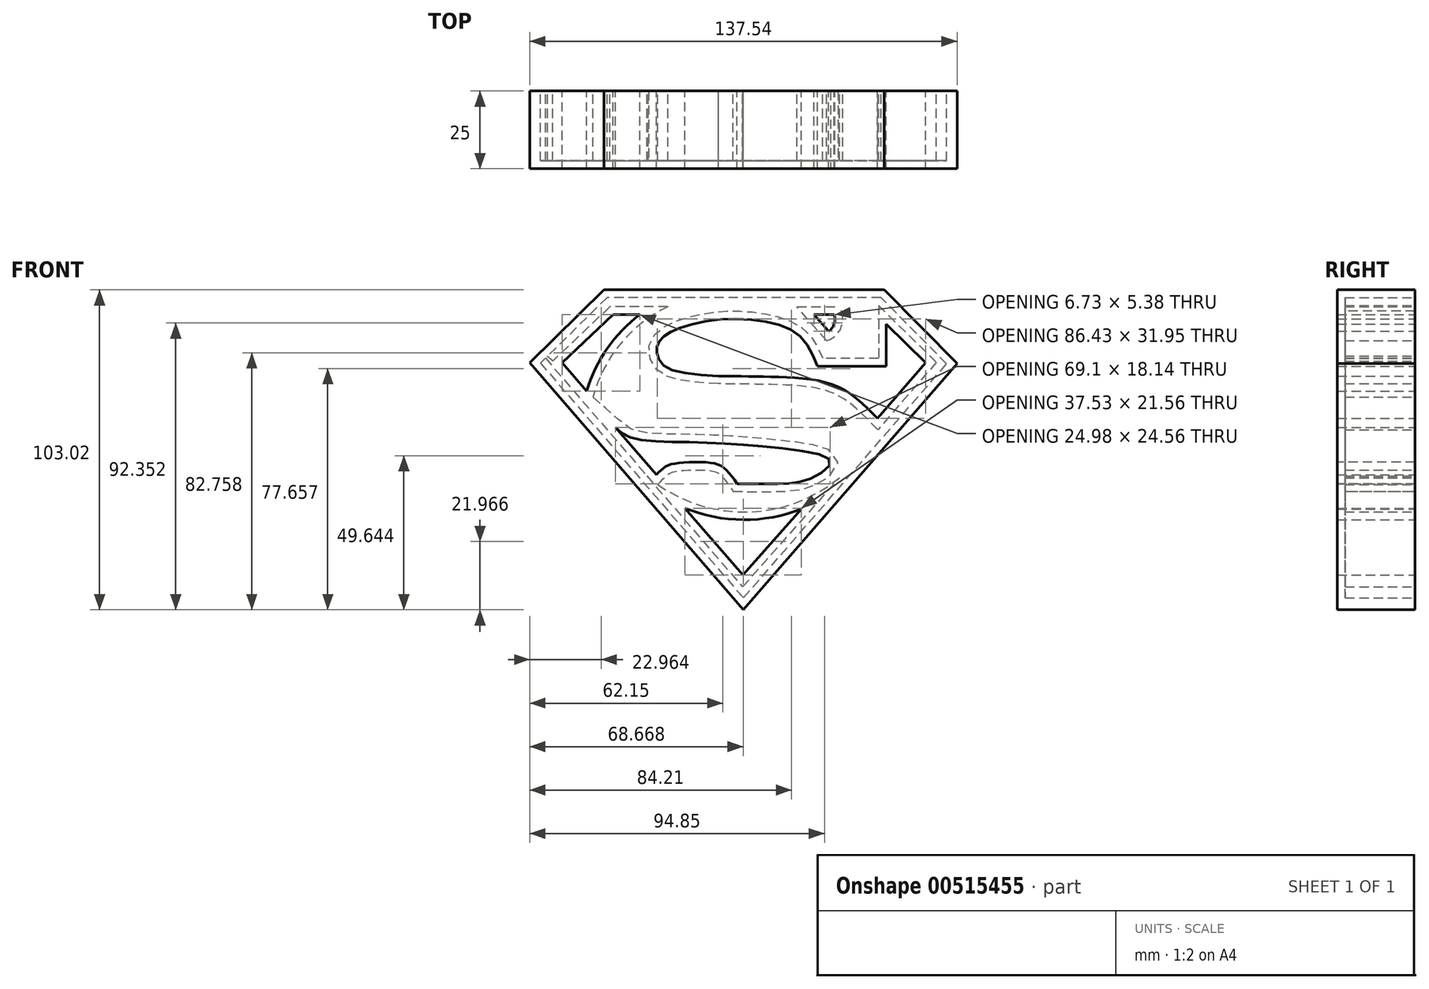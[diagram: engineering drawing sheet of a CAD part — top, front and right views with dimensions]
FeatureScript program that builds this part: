
annotation { "Feature Type Name" : "Feature", "Feature Type Description" : "" }
export const myFeature = defineFeature(function(context is Context, id is Id, definition is map)
    precondition{}
    {
        {
            var Q0;
            Q0=qCreatedBy(makeId("Front.planeOp"),FACE);
            var sketch = newSketch(context, id + "F0", { "sketchPlane" : qUnion([Q0])});
            skLineSegment(sketch, "E0", {"start": v(-66.75, 24.24) * mm, "end": v(2.02, -55.32) * mm});
            skLineSegment(sketch, "E1", {"start": v(2.02, -55.32) * mm, "end": v(70.79, 24) * mm});
            skLineSegment(sketch, "E2", {"start": v(70.79, 24) * mm, "end": v(47.3, 47.7) * mm});
            skLineSegment(sketch, "E3", {"start": v(47.3, 47.7) * mm, "end": v(-42.87, 47.7) * mm});
            skLineSegment(sketch, "E4", {"start": v(-42.87, 47.7) * mm, "end": v(-66.75, 24.24) * mm});
            skLineSegment(sketch, "E5", {"start": v(-56.28, 24.24) * mm, "end": v(-48.42, 15.16) * mm});
            skArc(sketch, "E6", {"start": v(-31.3, 39.72) * mm, "mid": v(-41.85, 28.83) * mm, "end": v(-48.42, 15.16) * mm});
            skLineSegment(sketch, "E7", {"start": v(-31.3, 39.72) * mm, "end": v(-40, 39.72) * mm});
            skLineSegment(sketch, "E8", {"start": v(-40, 39.72) * mm, "end": v(-56.28, 24.24) * mm});
            skLineSegment(sketch, "E9", {"start": v(29.39, 34.34) * mm, "end": v(24.74, 39.72) * mm});
            skLineSegment(sketch, "E10", {"start": v(24.74, 39.72) * mm, "end": v(31.24, 39.72) * mm});
            skArc(sketch, "E11", {"start": v(29.39, 34.34) * mm, "mid": v(31.2, 36.72) * mm, "end": v(31.24, 39.72) * mm});
            skLineSegment(sketch, "E12", {"start": v(-39.15, 3.4) * mm, "end": v(-26.01, -11.83) * mm});
            skLineSegment(sketch, "E13", {"start": v(-16.85, -22.57) * mm, "end": v(1.79, -44.13) * mm});
            skLineSegment(sketch, "E14", {"start": v(1.79, -44.13) * mm, "end": v(20.68, -22.86) * mm});
            skArc(sketch, "E15", {"start": v(-16.85, -22.57) * mm, "mid": v(1.9, -26.31) * mm, "end": v(20.68, -22.86) * mm});
            skLineSegment(sketch, "E16", {"start": v(48, 36.72) * mm, "end": v(60.67, 24.22) * mm});
            skLineSegment(sketch, "E17", {"start": v(60.67, 24.22) * mm, "end": v(45.14, 6.36) * mm});
            skLineSegment(sketch, "E18", {"start": v(48, 36.72) * mm, "end": v(48, 23.15) * mm});
            skLineSegment(sketch, "E19", {"start": v(48, 23.15) * mm, "end": v(25.86, 23.15) * mm});
            skFitSpline(sketch, "E20", {"points": [v(-26.01, -11.83) * mm, v(-23.24, -9.35) * mm, v(-19.32, -8.1) * mm, v(-8.96, -7.92) * mm, v(-4.32, -9.53) * mm, v(0, -14.7) * mm], "startDerivative": vector(16.73, 17.25) * mm, "endDerivative": vector(19.62, -27.74) * mm});
            skFitSpline(sketch, "E21", {"points": [v(0, -14.7) * mm, v(14.25, -14.7) * mm, v(23.9, -12.92) * mm, v(29.96, -7.56) * mm, v(12.29, -3.1) * mm, v(-15.39, -1.32) * mm, v(-33.78, 0) * mm, v(-39.15, 3.4) * mm], "startDerivative": vector(104.56, -1.27) * mm, "endDerivative": vector(-45.28, 40.5) * mm});
            skFitSpline(sketch, "E22", {"points": [v(45.14, 6.36) * mm, v(32.1, 16.65) * mm, v(12.9, 19.65) * mm, v(-6, 19.95) * mm], "startDerivative": vector(-37.24, 37.96) * mm, "endDerivative": vector(-54.73, 0.43) * mm});
            skFitSpline(sketch, "E23", {"points": [v(-6, 19.95) * mm, v(-22.72, 22.66) * mm, v(-25.56, 26.26) * mm, v(-25.93, 29.1) * mm, v(-24.42, 31.93) * mm, v(-20.45, 34.58) * mm, v(-7.6, 37.98) * mm, v(10.18, 37.22) * mm, v(20.77, 32.3) * mm, v(25.86, 23.15) * mm], "startDerivative": vector(-130.14, 8.1) * mm, "endDerivative": vector(33.04, -82.79) * mm});
            skSolve(sketch);
        }
        {
            var Q0;
            Q0=makeQuery(id+"F0.imprint","IMPRINT",FACE,{"disambiguationData":[TD([[makeQuery(id+"F0.imprint","IMPRINT",EDGE,{"derivedFrom":sQuery(id+"F0.wireOp",EDGE,"E0")}),1.0]])]});
            extrude(context, id + "F1", {"entities" : qUnion([Q0]), "depth" : 25 * mm, "offsetDistance" : 25 * mm});
        }
        {
            var Q0;
            Q0=makeQuery(id+"F1.opExtrude","CAP_FACE",FACE,{"disambiguationData":[OSD([sQuery(id+"F0.wireOp",EDGE,"E0"),sQuery(id+"F0.wireOp",EDGE,"E1"),sQuery(id+"F0.wireOp",EDGE,"E2"),sQuery(id+"F0.wireOp",EDGE,"E3"),sQuery(id+"F0.wireOp",EDGE,"E4"),sQuery(id+"F0.wireOp",EDGE,"E5"),sQuery(id+"F0.wireOp",EDGE,"E6"),sQuery(id+"F0.wireOp",EDGE,"E7"),sQuery(id+"F0.wireOp",EDGE,"E8"),sQuery(id+"F0.wireOp",EDGE,"E9"),sQuery(id+"F0.wireOp",EDGE,"E10"),sQuery(id+"F0.wireOp",EDGE,"E11"),sQuery(id+"F0.wireOp",EDGE,"E12"),sQuery(id+"F0.wireOp",EDGE,"E13"),sQuery(id+"F0.wireOp",EDGE,"E14"),sQuery(id+"F0.wireOp",EDGE,"E15"),sQuery(id+"F0.wireOp",EDGE,"E16"),sQuery(id+"F0.wireOp",EDGE,"E17"),sQuery(id+"F0.wireOp",EDGE,"E18"),sQuery(id+"F0.wireOp",EDGE,"E19"),sQuery(id+"F0.wireOp",EDGE,"E20"),sQuery(id+"F0.wireOp",EDGE,"E21"),sQuery(id+"F0.wireOp",EDGE,"E22"),sQuery(id+"F0.wireOp",EDGE,"E23")])],"isStart":true});
            shell(context, id + "F2", {"entities" : qUnion([Q0]), "thickness" : 2.5 * mm});
        }
    });
